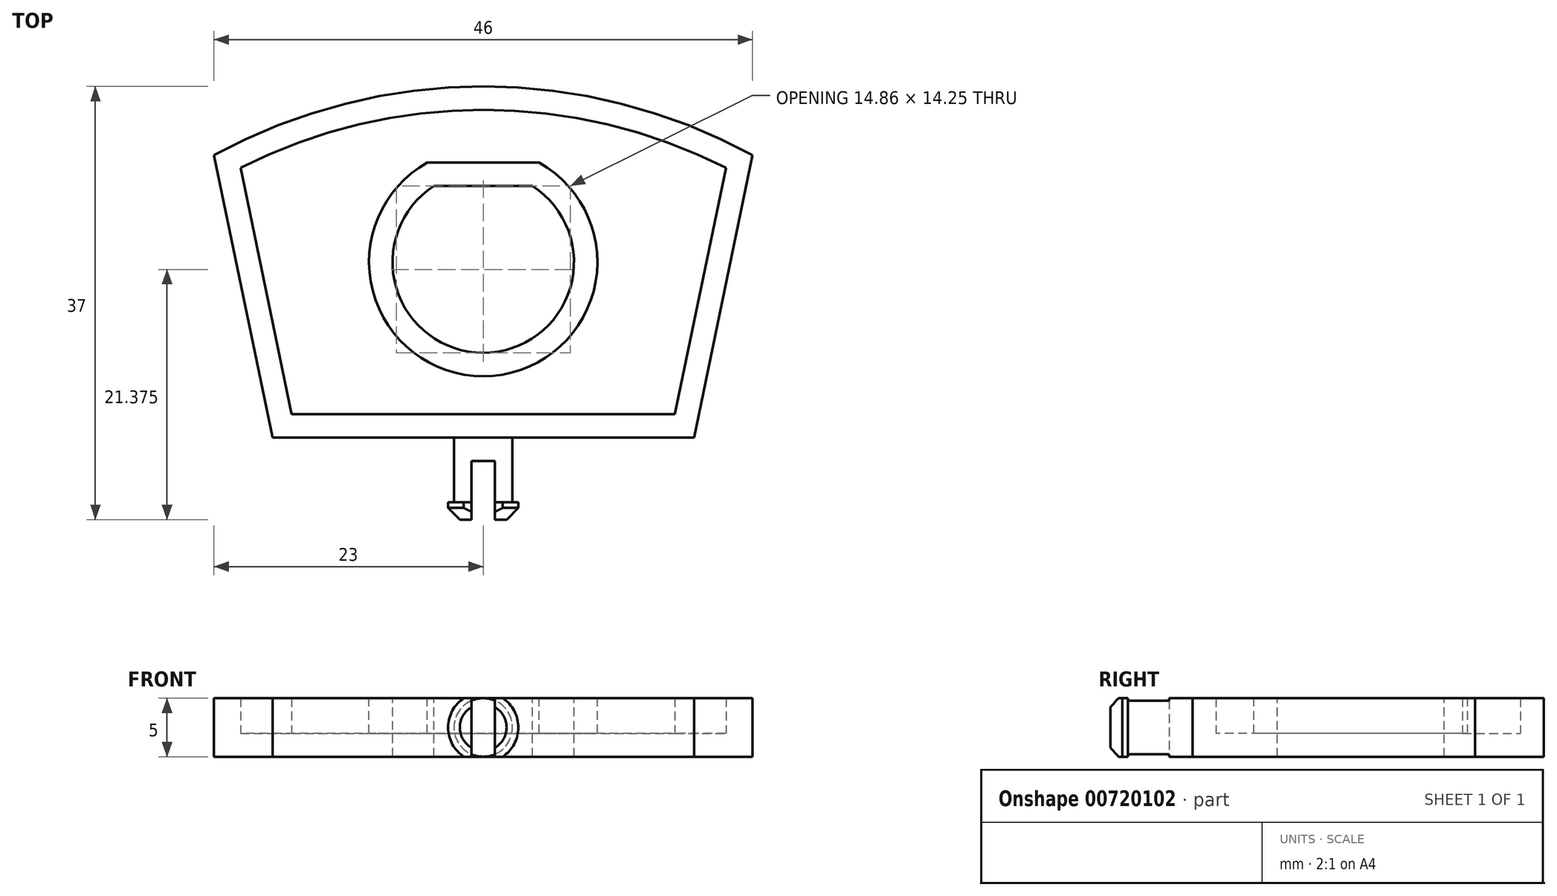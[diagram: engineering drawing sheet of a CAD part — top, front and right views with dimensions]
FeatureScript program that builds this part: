
annotation { "Feature Type Name" : "Feature", "Feature Type Description" : "" }
export const myFeature = defineFeature(function(context is Context, id is Id, definition is map)
    precondition{}
    {
        {
            var Q0;
            Q0=qCreatedBy(makeId("Top.planeOp"),FACE);
            var sketch = newSketch(context, id + "F0", { "sketchPlane" : qUnion([Q0])});
            skLineSegment(sketch, "E0", {"start": v(-23, 24.13) * mm, "end": v(-18, 0) * mm});
            skLineSegment(sketch, "E1", {"start": v(-18, 0) * mm, "end": v(18, 0) * mm});
            skLineSegment(sketch, "E2", {"start": v(18, 0) * mm, "end": v(23, 24.13) * mm});
            skArc(sketch, "E3", {"start": v(23, 24.13) * mm, "mid": v(0, 30) * mm, "end": v(-23, 24.13) * mm});
            skSolve(sketch);
        }
        {
            var Q0;
            Q0=makeQuery(id+"F0.imprint","IMPRINT",FACE,{"disambiguationData":[TD([[makeQuery(id+"F0.imprint","IMPRINT",EDGE,{"derivedFrom":sQuery(id+"F0.wireOp",EDGE,"E0")}),1.0]])]});
            extrude(context, id + "F1", {"entities" : qUnion([Q0]), "endBound" : BoundingType.SYMMETRIC, "depth" : 5 * mm, "offsetDistance" : 25 * mm});
        }
        {
            var Q0;
            Q0=makeQuery(id+"F1.opExtrude","CAP_FACE",FACE,{"disambiguationData":[OSD([sQuery(id+"F0.wireOp",EDGE,"E0"),sQuery(id+"F0.wireOp",EDGE,"E1"),sQuery(id+"F0.wireOp",EDGE,"E2"),sQuery(id+"F0.wireOp",EDGE,"E3")])],"isStart":false});
            var sketch = newSketch(context, id + "F2", { "sketchPlane" : qUnion([Q0])});
            skLineSegment(sketch, "E4", {"start": v(-4.22, 21.5) * mm, "end": v(4.22, 21.5) * mm});
            skArc(sketch, "E5", {"start": v(-4.22, 21.5) * mm, "mid": v(0, 7.25) * mm, "end": v(4.22, 21.5) * mm});
            skSolve(sketch);
        }
        {
            var Q0;
            Q0=makeQuery(id+"F2.imprint","IMPRINT",FACE,{"disambiguationData":[TD([[makeQuery(id+"F2.imprint","IMPRINT",EDGE,{"derivedFrom":sQuery(id+"F2.wireOp",EDGE,"E4")}),-1.0]])]});
            extrude(context, id + "F3", {"entities" : qUnion([Q0]), "operationType" : NewBodyOperationType.REMOVE, "endBound" : BoundingType.UP_TO_NEXT, "oppositeDirection" : true, "depth" : 25 * mm, "offsetDistance" : 25 * mm});
        }
        {
            var Q0;
            Q0=makeQuery(id+"F1.opExtrude","CAP_FACE",FACE,{"disambiguationData":[OSD([sQuery(id+"F0.wireOp",EDGE,"E0"),sQuery(id+"F0.wireOp",EDGE,"E1"),sQuery(id+"F0.wireOp",EDGE,"E2"),sQuery(id+"F0.wireOp",EDGE,"E3")])],"isStart":false});
            shell(context, id + "F4", {"entities" : qUnion([Q0]), "thickness" : 2 * mm});
        }
        {
            var Q0;
            Q0=qCreatedBy(makeId("Right.planeOp"),FACE);
            var sketch = newSketch(context, id + "F5", { "sketchPlane" : qUnion([Q0])});
            skLineSegment(sketch, "E6", {"start": v(0, 0) * mm, "end": v(-7, 0) * mm});
            skLineSegment(sketch, "E7", {"start": v(-7, 0) * mm, "end": v(-7, 3) * mm});
            skLineSegment(sketch, "E8", {"start": v(-7, 3) * mm, "end": v(-5.5, 3) * mm});
            skLineSegment(sketch, "E9", {"start": v(-5.5, 3) * mm, "end": v(-5.5, 2.5) * mm});
            skLineSegment(sketch, "E10", {"start": v(-5.5, 2.5) * mm, "end": v(0, 2.5) * mm});
            skLineSegment(sketch, "E11", {"start": v(0, 2.5) * mm, "end": v(0, 0) * mm});
            skSolve(sketch);
        }
        {
            var Q0;
            Q0=makeQuery(id+"F5.imprint","IMPRINT",FACE,{"disambiguationData":[TD([[makeQuery(id+"F5.imprint","IMPRINT",EDGE,{"derivedFrom":sQuery(id+"F5.wireOp",EDGE,"E6")}),-1.0]])]});
            var Q1;
            Q1=sQuery(id+"F5.wireOp",EDGE,"E6");
            revolve(context, id + "F6", {"operationType" : NewBodyOperationType.ADD, "surfaceOperationType" : NewSurfaceOperationType.NEW, "entities" : qUnion([Q0]), "axis" : qUnion([Q1]), "revolveType" : RevolveType.FULL});
        }
        {
            var Q0;
            Q0=makeQuery(id+"F6.opRevolve","SWEPT_FACE",FACE,{"disambiguationData":[OSD([sQuery(id+"F5.wireOp",EDGE,"E7")])]});
            chamfer(context, id + "F7", {"entities" : qUnion([Q0]), "width" : 1 * mm});
        }
        {
            var Q0;
            Q0=makeQuery(id+"F6.opRevolve","SWEPT_FACE",FACE,{"disambiguationData":[OSD([sQuery(id+"F5.wireOp",EDGE,"E7")])]});
            var sketch = newSketch(context, id + "F8", { "sketchPlane" : qUnion([Q0])});
            skLineSegment(sketch, "E12.bottom", {"start": v(-24.5, 2.5) * mm, "end": v(25.95, 2.5) * mm});
            skLineSegment(sketch, "E12.top", {"start": v(-24.5, -2.5) * mm, "end": v(25.95, -2.5) * mm});
            skLineSegment(sketch, "E12.left", {"start": v(-24.5, 2.5) * mm, "end": v(-24.5, -2.5) * mm});
            skLineSegment(sketch, "E12.right", {"start": v(25.95, 2.5) * mm, "end": v(25.95, -2.5) * mm});
            skSolve(sketch);
        }
        {
            var Q0;
            Q0 = qSketchRegion(id + "F8", true);
            extrude(context, id + "F9", {"entities" : qUnion([Q0]), "operationType" : NewBodyOperationType.INTERSECT, "endBound" : BoundingType.THROUGH_ALL, "oppositeDirection" : true, "depth" : 25 * mm, "offsetDistance" : 25 * mm});
        }
        {
            var Q0;
            Q0=makeQuery(id+"F6.opRevolve","SWEPT_FACE",FACE,{"disambiguationData":[OSD([sQuery(id+"F5.wireOp",EDGE,"E7")])]});
            var sketch = newSketch(context, id + "F10", { "sketchPlane" : qUnion([Q0])});
            skLineSegment(sketch, "E13.bottom", {"start": v(-1, 4.63) * mm, "end": v(1, 4.63) * mm});
            skLineSegment(sketch, "E13.top", {"start": v(-1, -4.89) * mm, "end": v(1, -4.89) * mm});
            skLineSegment(sketch, "E13.left", {"start": v(-1, 4.63) * mm, "end": v(-1, -4.89) * mm});
            skLineSegment(sketch, "E13.right", {"start": v(1, 4.63) * mm, "end": v(1, -4.89) * mm});
            skSolve(sketch);
        }
        {
            var Q0;
            {var subQ0=sQuery(id+"F10.wireOp",EDGE,"E13.top");Q0=makeQuery(id+"F10.imprint","IMPRINT",FACE,{"disambiguationData":[TD([[makeQuery(id+"F10.imprint","IMPRINT",EDGE,{"derivedFrom":subQ0}),1.0]])]});}
            var Q1;
            {var subQ0=sQuery(id+"F10.wireOp",EDGE,"E13.left");var subQ1=sQuery(id+"F5.wireOp",EDGE,"E7");var subQ2=makeQuery(id+"F7.opChamfer","BLEND_EDGE",EDGE,{"blendedFrom":[makeQuery(id+"F6.opRevolve","SWEPT_EDGE",EDGE,{"disambiguationData":[OSD([subQ1,sQuery(id+"F5.wireOp",EDGE,"E8")])]}),makeQuery(id+"F6.opRevolve","SWEPT_FACE",FACE,{"disambiguationData":[OSD([subQ1])]})],"blendedInto":[makeQuery(id+"F6.opRevolve","SWEPT_FACE",FACE,{"disambiguationData":[OSD([subQ1])]})]});var subQ3=makeQuery(id+"F10.imprint","INTERSECT",VERTEX,{"disambiguationData":[OD(0.0)],"derivedFrom":[subQ2,subQ0]});Q1=makeQuery(id+"F10.imprint","IMPRINT",FACE,{"disambiguationData":[TD([[makeQuery(id+"F10.imprint","IMPRINT",EDGE,{"disambiguationData":[TD([[subQ3,-1.0]])],"derivedFrom":subQ0}),1.0]])]});}
            var Q2;
            {var subQ0=sQuery(id+"F10.wireOp",EDGE,"E13.bottom");Q2=makeQuery(id+"F10.imprint","IMPRINT",FACE,{"disambiguationData":[TD([[makeQuery(id+"F10.imprint","IMPRINT",EDGE,{"derivedFrom":subQ0}),-1.0]])]});}
            extrude(context, id + "F11", {"entities" : qUnion([Q0, Q1, Q2]), "operationType" : NewBodyOperationType.REMOVE, "oppositeDirection" : true, "depth" : 5 * mm, "offsetDistance" : 25 * mm});
        }
    });
